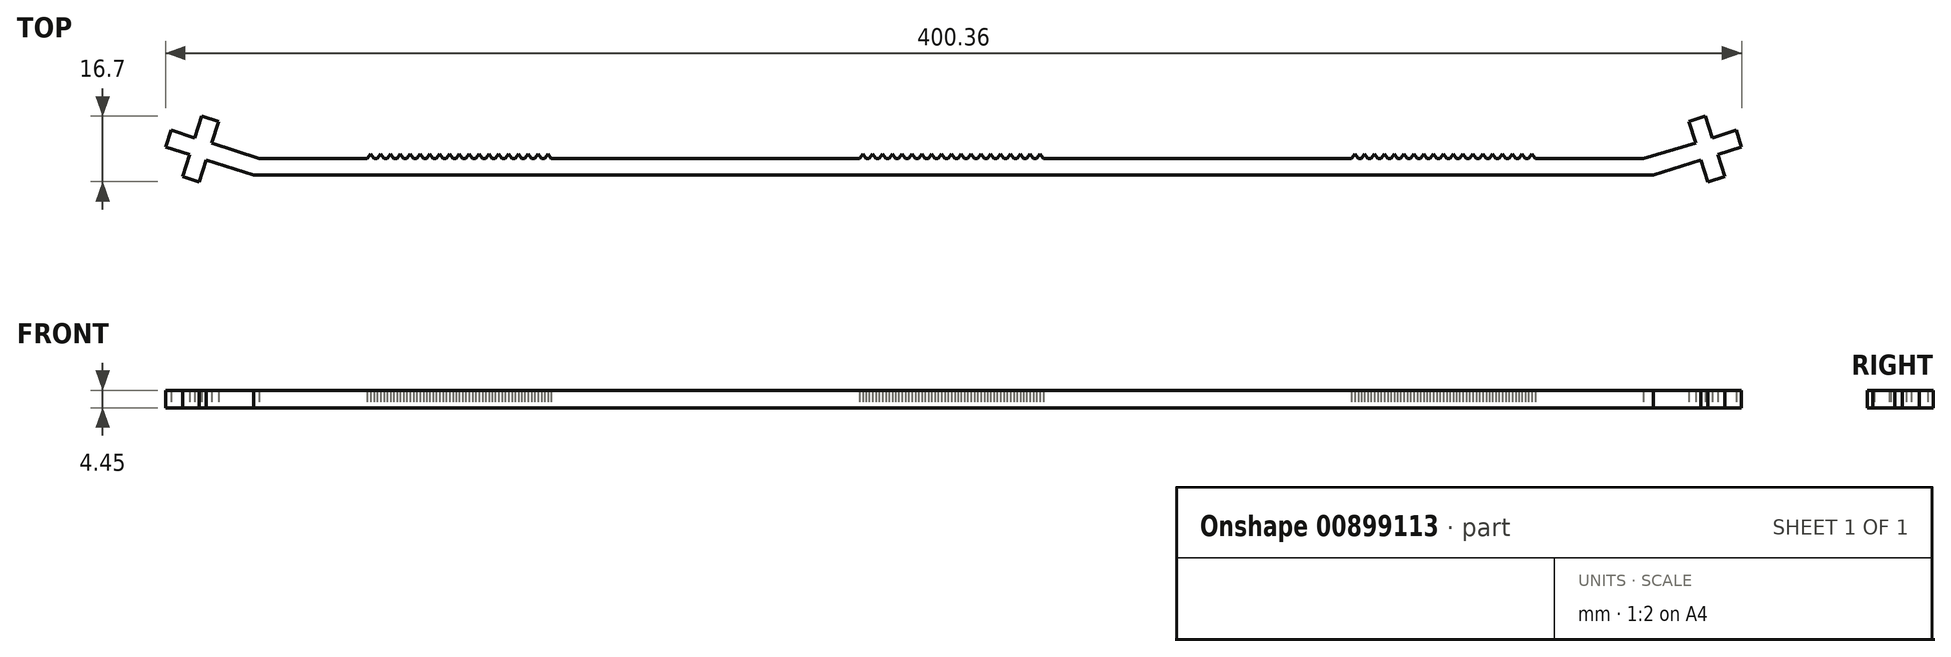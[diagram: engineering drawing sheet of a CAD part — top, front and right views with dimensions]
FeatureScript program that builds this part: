
annotation { "Feature Type Name" : "Feature", "Feature Type Description" : "" }
export const myFeature = defineFeature(function(context is Context, id is Id, definition is map)
    precondition{}
    {
        {
            var Q0;
            Q0=qCreatedBy(makeId("Top.planeOp"),FACE);
            var sketch = newSketch(context, id + "F0", { "sketchPlane" : qUnion([Q0])});
            skLineSegment(sketch, "E0", {"start": v(-319.35, 28.42) * mm, "end": v(36.25, 28.42) * mm});
            skLineSegment(sketch, "E1", {"start": v(-319.35, 28.42) * mm, "end": v(-331.45, 32.3) * mm});
            skLineSegment(sketch, "E2", {"start": v(-331.45, 32.3) * mm, "end": v(-333.23, 26.75) * mm});
            skLineSegment(sketch, "E3", {"start": v(-333.23, 26.75) * mm, "end": v(-337.46, 28.1) * mm});
            skLineSegment(sketch, "E4", {"start": v(-337.46, 28.1) * mm, "end": v(-335.68, 33.66) * mm});
            skLineSegment(sketch, "E5", {"start": v(-335.68, 33.66) * mm, "end": v(-341.73, 35.6) * mm});
            skLineSegment(sketch, "E6", {"start": v(-341.73, 35.6) * mm, "end": v(-340.37, 39.84) * mm});
            skLineSegment(sketch, "E7", {"start": v(-340.37, 39.84) * mm, "end": v(-334.32, 37.9) * mm});
            skLineSegment(sketch, "E8", {"start": v(-334.32, 37.9) * mm, "end": v(-332.54, 43.45) * mm});
            skLineSegment(sketch, "E9", {"start": v(-332.54, 43.45) * mm, "end": v(-328.3, 42.09) * mm});
            skLineSegment(sketch, "E10", {"start": v(-328.3, 42.09) * mm, "end": v(-330.09, 36.54) * mm});
            skLineSegment(sketch, "E11", {"start": v(-330.09, 36.54) * mm, "end": v(-318, 32.66) * mm});
            skLineSegment(sketch, "E12", {"start": v(-318, 32.66) * mm, "end": v(-290.5, 32.66) * mm});
            skLineSegment(sketch, "E13", {"start": v(-142.13, 33.8) * mm, "end": v(-141.27, 32.66) * mm});
            skLineSegment(sketch, "E14.MirrorCS", {"start": v(-142.13, 33.8) * mm, "end": v(-143, 32.66) * mm});
            skLineSegment(sketch, "E15.trimOffspring", {"start": v(-141.27, 32.66) * mm, "end": v(-140.5, 32.66) * mm});
            skPoint(sketch, "E16.start.orphan", {"position": v(-141.55, 28.42) * mm});
            skLineSegment(sketch, "E17.direction1", {"start": v(-141.27, 32.66) * mm, "end": v(-140.5, 32.66) * mm, "construction": true});
            skLineSegment(sketch, "E18.1.0.0", {"start": v(-139.63, 33.8) * mm, "end": v(-138.77, 32.66) * mm});
            skLineSegment(sketch, "E18.1.0.1", {"start": v(-139.63, 33.8) * mm, "end": v(-140.5, 32.66) * mm});
            skLineSegment(sketch, "E18.2.0.0", {"start": v(-137.13, 33.8) * mm, "end": v(-136.27, 32.66) * mm});
            skLineSegment(sketch, "E18.2.0.1", {"start": v(-137.13, 33.8) * mm, "end": v(-138, 32.66) * mm});
            skLineSegment(sketch, "E18.3.0.0", {"start": v(-134.63, 33.8) * mm, "end": v(-133.77, 32.66) * mm});
            skLineSegment(sketch, "E18.3.0.1", {"start": v(-134.63, 33.8) * mm, "end": v(-135.5, 32.66) * mm});
            skLineSegment(sketch, "E18.4.0.0", {"start": v(-132.13, 33.8) * mm, "end": v(-131.27, 32.66) * mm});
            skLineSegment(sketch, "E18.4.0.1", {"start": v(-132.13, 33.8) * mm, "end": v(-133, 32.66) * mm});
            skLineSegment(sketch, "E18.5.0.0", {"start": v(-129.63, 33.8) * mm, "end": v(-128.77, 32.66) * mm});
            skLineSegment(sketch, "E18.5.0.1", {"start": v(-129.63, 33.8) * mm, "end": v(-130.5, 32.66) * mm});
            skLineSegment(sketch, "E18.6.0.0", {"start": v(-127.13, 33.8) * mm, "end": v(-126.27, 32.66) * mm});
            skLineSegment(sketch, "E18.6.0.1", {"start": v(-127.13, 33.8) * mm, "end": v(-128, 32.66) * mm});
            skLineSegment(sketch, "E18.7.0.0", {"start": v(-124.63, 33.8) * mm, "end": v(-123.77, 32.66) * mm});
            skLineSegment(sketch, "E18.7.0.1", {"start": v(-124.63, 33.8) * mm, "end": v(-125.5, 32.66) * mm});
            skLineSegment(sketch, "E18.8.0.0", {"start": v(-122.13, 33.8) * mm, "end": v(-121.27, 32.66) * mm});
            skLineSegment(sketch, "E18.8.0.1", {"start": v(-122.13, 33.8) * mm, "end": v(-123, 32.66) * mm});
            skLineSegment(sketch, "E18.9.0.0", {"start": v(-119.63, 33.8) * mm, "end": v(-118.77, 32.66) * mm});
            skLineSegment(sketch, "E18.9.0.1", {"start": v(-119.63, 33.8) * mm, "end": v(-120.5, 32.66) * mm});
            skLineSegment(sketch, "E19.1.0.0", {"start": v(-144.63, 33.8) * mm, "end": v(-145.5, 32.66) * mm});
            skLineSegment(sketch, "E19.1.0.1", {"start": v(-144.63, 33.8) * mm, "end": v(-143.77, 32.66) * mm});
            skLineSegment(sketch, "E19.2.0.0", {"start": v(-147.13, 33.8) * mm, "end": v(-148, 32.66) * mm});
            skLineSegment(sketch, "E19.2.0.1", {"start": v(-147.13, 33.8) * mm, "end": v(-146.27, 32.66) * mm});
            skLineSegment(sketch, "E19.3.0.0", {"start": v(-149.63, 33.8) * mm, "end": v(-150.5, 32.66) * mm});
            skLineSegment(sketch, "E19.3.0.1", {"start": v(-149.63, 33.8) * mm, "end": v(-148.77, 32.66) * mm});
            skLineSegment(sketch, "E19.4.0.0", {"start": v(-152.13, 33.8) * mm, "end": v(-153, 32.66) * mm});
            skLineSegment(sketch, "E19.4.0.1", {"start": v(-152.13, 33.8) * mm, "end": v(-151.27, 32.66) * mm});
            skLineSegment(sketch, "E19.5.0.0", {"start": v(-154.63, 33.8) * mm, "end": v(-155.5, 32.66) * mm});
            skLineSegment(sketch, "E19.5.0.1", {"start": v(-154.63, 33.8) * mm, "end": v(-153.77, 32.66) * mm});
            skLineSegment(sketch, "E19.6.0.0", {"start": v(-157.13, 33.8) * mm, "end": v(-158, 32.66) * mm});
            skLineSegment(sketch, "E19.6.0.1", {"start": v(-157.13, 33.8) * mm, "end": v(-156.27, 32.66) * mm});
            skLineSegment(sketch, "E19.7.0.0", {"start": v(-159.63, 33.8) * mm, "end": v(-160.5, 32.66) * mm});
            skLineSegment(sketch, "E19.7.0.1", {"start": v(-159.63, 33.8) * mm, "end": v(-158.77, 32.66) * mm});
            skLineSegment(sketch, "E19.8.0.0", {"start": v(-162.13, 33.8) * mm, "end": v(-163, 32.66) * mm});
            skLineSegment(sketch, "E19.8.0.1", {"start": v(-162.13, 33.8) * mm, "end": v(-161.27, 32.66) * mm});
            skLineSegment(sketch, "E19.9.0.0", {"start": v(-164.63, 33.8) * mm, "end": v(-165.5, 32.66) * mm});
            skLineSegment(sketch, "E19.9.0.1", {"start": v(-164.63, 33.8) * mm, "end": v(-163.77, 32.66) * mm});
            skLineSegment(sketch, "E19.direction1", {"start": v(-143, 32.66) * mm, "end": v(-143.77, 32.66) * mm, "construction": true});
            skLineSegment(sketch, "E20.trimOffspring", {"start": v(-163.77, 32.66) * mm, "end": v(-163, 32.66) * mm});
            skLineSegment(sketch, "E21.trimOffspring", {"start": v(-161.27, 32.66) * mm, "end": v(-160.5, 32.66) * mm});
            skLineSegment(sketch, "E22.trimOffspring", {"start": v(-158.77, 32.66) * mm, "end": v(-158, 32.66) * mm});
            skLineSegment(sketch, "E23.trimOffspring", {"start": v(-153.77, 32.66) * mm, "end": v(-153, 32.66) * mm});
            skLineSegment(sketch, "E24.trimOffspring", {"start": v(-156.27, 32.66) * mm, "end": v(-155.5, 32.66) * mm});
            skLineSegment(sketch, "E25.trimOffspring", {"start": v(-151.27, 32.66) * mm, "end": v(-150.5, 32.66) * mm});
            skLineSegment(sketch, "E26.trimOffspring", {"start": v(-148.77, 32.66) * mm, "end": v(-148, 32.66) * mm});
            skLineSegment(sketch, "E27.trimOffspring", {"start": v(-146.27, 32.66) * mm, "end": v(-145.5, 32.66) * mm});
            skLineSegment(sketch, "E28.trimOffspring", {"start": v(-143.77, 32.66) * mm, "end": v(-143, 32.66) * mm});
            skLineSegment(sketch, "E29.trimOffspring", {"start": v(-138.77, 32.66) * mm, "end": v(-138, 32.66) * mm, "construction": true});
            skLineSegment(sketch, "E30.trimOffspring", {"start": v(-138.77, 32.66) * mm, "end": v(-138, 32.66) * mm});
            skLineSegment(sketch, "E31.trimOffspring", {"start": v(-136.27, 32.66) * mm, "end": v(-135.5, 32.66) * mm, "construction": true});
            skLineSegment(sketch, "E32.trimOffspring", {"start": v(-136.27, 32.66) * mm, "end": v(-135.5, 32.66) * mm});
            skLineSegment(sketch, "E33.trimOffspring", {"start": v(-133.77, 32.66) * mm, "end": v(-133, 32.66) * mm, "construction": true});
            skLineSegment(sketch, "E34.trimOffspring", {"start": v(-131.27, 32.66) * mm, "end": v(-130.5, 32.66) * mm, "construction": true});
            skLineSegment(sketch, "E35.trimOffspring", {"start": v(-131.27, 32.66) * mm, "end": v(-130.5, 32.66) * mm});
            skLineSegment(sketch, "E36", {"start": v(-133.77, 32.66) * mm, "end": v(-133, 32.66) * mm});
            skLineSegment(sketch, "E37.trimOffspring", {"start": v(-128.77, 32.66) * mm, "end": v(-128, 32.66) * mm, "construction": true});
            skLineSegment(sketch, "E38.trimOffspring", {"start": v(-128.77, 32.66) * mm, "end": v(-128, 32.66) * mm});
            skLineSegment(sketch, "E39.trimOffspring", {"start": v(-126.27, 32.66) * mm, "end": v(-125.5, 32.66) * mm, "construction": true});
            skLineSegment(sketch, "E40.trimOffspring", {"start": v(-126.27, 32.66) * mm, "end": v(-125.5, 32.66) * mm});
            skLineSegment(sketch, "E41.trimOffspring", {"start": v(-123.77, 32.66) * mm, "end": v(-123, 32.66) * mm, "construction": true});
            skLineSegment(sketch, "E42.trimOffspring", {"start": v(-123.77, 32.66) * mm, "end": v(-123, 32.66) * mm});
            skLineSegment(sketch, "E43.trimOffspring", {"start": v(-121.27, 32.66) * mm, "end": v(-120.5, 32.66) * mm, "construction": true});
            skLineSegment(sketch, "E44.trimOffspring", {"start": v(-121.27, 32.66) * mm, "end": v(-120.5, 32.66) * mm});
            skLineSegment(sketch, "E45.trimOffspring", {"start": v(-118.77, 32.66) * mm, "end": v(-116.27, 32.66) * mm, "construction": true});
            skLineSegment(sketch, "E46.trimOffspring", {"start": v(-118.77, 32.66) * mm, "end": v(-40.5, 32.66) * mm});
            skLineSegment(sketch, "E47.1.0.0", {"start": v(5.37, 33.8) * mm, "end": v(6.23, 32.66) * mm});
            skLineSegment(sketch, "E47.1.0.1", {"start": v(5.37, 33.8) * mm, "end": v(4.5, 32.66) * mm});
            skLineSegment(sketch, "E47.1.0.2", {"start": v(2.87, 33.8) * mm, "end": v(3.73, 32.66) * mm});
            skLineSegment(sketch, "E47.1.0.3", {"start": v(2.87, 33.8) * mm, "end": v(2, 32.66) * mm});
            skLineSegment(sketch, "E47.1.0.4", {"start": v(0.37, 33.8) * mm, "end": v(1.23, 32.66) * mm});
            skLineSegment(sketch, "E47.1.0.5", {"start": v(0.37, 33.8) * mm, "end": v(-0.5, 32.66) * mm});
            skLineSegment(sketch, "E47.1.0.6", {"start": v(-2.13, 33.8) * mm, "end": v(-1.27, 32.66) * mm});
            skLineSegment(sketch, "E47.1.0.7", {"start": v(-2.13, 33.8) * mm, "end": v(-3, 32.66) * mm});
            skLineSegment(sketch, "E47.1.0.8", {"start": v(-4.63, 33.8) * mm, "end": v(-3.77, 32.66) * mm});
            skLineSegment(sketch, "E47.1.0.9", {"start": v(-4.63, 33.8) * mm, "end": v(-5.5, 32.66) * mm});
            skLineSegment(sketch, "E47.1.0.10", {"start": v(-7.13, 33.8) * mm, "end": v(-6.27, 32.66) * mm});
            skLineSegment(sketch, "E47.1.0.11", {"start": v(-7.13, 33.8) * mm, "end": v(-8, 32.66) * mm});
            skLineSegment(sketch, "E47.1.0.12", {"start": v(-9.63, 33.8) * mm, "end": v(-8.77, 32.66) * mm});
            skLineSegment(sketch, "E47.1.0.13", {"start": v(-9.63, 33.8) * mm, "end": v(-10.5, 32.66) * mm});
            skLineSegment(sketch, "E47.1.0.14", {"start": v(-12.13, 33.8) * mm, "end": v(-11.27, 32.66) * mm});
            skLineSegment(sketch, "E47.1.0.15", {"start": v(-12.13, 33.8) * mm, "end": v(-13, 32.66) * mm});
            skLineSegment(sketch, "E47.1.0.16", {"start": v(-14.63, 33.8) * mm, "end": v(-13.77, 32.66) * mm});
            skLineSegment(sketch, "E47.1.0.17", {"start": v(-14.63, 33.8) * mm, "end": v(-15.5, 32.66) * mm});
            skLineSegment(sketch, "E47.1.0.18", {"start": v(-17.13, 33.8) * mm, "end": v(-16.27, 32.66) * mm});
            skLineSegment(sketch, "E47.1.0.19", {"start": v(-17.13, 33.8) * mm, "end": v(-18, 32.66) * mm});
            skLineSegment(sketch, "E47.1.0.20", {"start": v(-19.63, 33.8) * mm, "end": v(-18.77, 32.66) * mm});
            skLineSegment(sketch, "E47.1.0.21", {"start": v(-19.63, 33.8) * mm, "end": v(-20.5, 32.66) * mm});
            skLineSegment(sketch, "E47.1.0.22", {"start": v(-22.13, 33.8) * mm, "end": v(-21.27, 32.66) * mm});
            skLineSegment(sketch, "E47.1.0.23", {"start": v(-22.13, 33.8) * mm, "end": v(-23, 32.66) * mm});
            skLineSegment(sketch, "E47.1.0.24", {"start": v(-24.63, 33.8) * mm, "end": v(-23.77, 32.66) * mm});
            skLineSegment(sketch, "E47.1.0.25", {"start": v(-24.63, 33.8) * mm, "end": v(-25.5, 32.66) * mm});
            skLineSegment(sketch, "E47.1.0.26", {"start": v(-27.13, 33.8) * mm, "end": v(-26.27, 32.66) * mm});
            skLineSegment(sketch, "E47.1.0.27", {"start": v(-27.13, 33.8) * mm, "end": v(-28, 32.66) * mm});
            skLineSegment(sketch, "E47.1.0.28", {"start": v(-29.63, 33.8) * mm, "end": v(-28.77, 32.66) * mm});
            skLineSegment(sketch, "E47.1.0.29", {"start": v(-29.63, 33.8) * mm, "end": v(-30.5, 32.66) * mm});
            skLineSegment(sketch, "E47.1.0.30", {"start": v(-32.13, 33.8) * mm, "end": v(-31.27, 32.66) * mm});
            skLineSegment(sketch, "E47.1.0.31", {"start": v(-32.13, 33.8) * mm, "end": v(-33, 32.66) * mm});
            skLineSegment(sketch, "E47.1.0.32", {"start": v(-34.63, 33.8) * mm, "end": v(-33.77, 32.66) * mm});
            skLineSegment(sketch, "E47.1.0.33", {"start": v(-34.63, 33.8) * mm, "end": v(-35.5, 32.66) * mm});
            skLineSegment(sketch, "E47.1.0.34", {"start": v(-37.13, 33.8) * mm, "end": v(-36.27, 32.66) * mm});
            skLineSegment(sketch, "E47.1.0.35", {"start": v(-37.13, 33.8) * mm, "end": v(-38, 32.66) * mm});
            skLineSegment(sketch, "E47.1.0.36", {"start": v(-39.63, 33.8) * mm, "end": v(-38.77, 32.66) * mm});
            skLineSegment(sketch, "E47.1.0.37", {"start": v(-39.63, 33.8) * mm, "end": v(-40.5, 32.66) * mm});
            skLineSegment(sketch, "E48.1.0.0", {"start": v(-244.63, 33.8) * mm, "end": v(-243.77, 32.66) * mm});
            skLineSegment(sketch, "E48.1.0.1", {"start": v(-244.63, 33.8) * mm, "end": v(-245.5, 32.66) * mm});
            skLineSegment(sketch, "E48.1.0.2", {"start": v(-247.13, 33.8) * mm, "end": v(-246.27, 32.66) * mm});
            skLineSegment(sketch, "E48.1.0.3", {"start": v(-247.13, 33.8) * mm, "end": v(-248, 32.66) * mm});
            skLineSegment(sketch, "E48.1.0.4", {"start": v(-249.63, 33.8) * mm, "end": v(-248.77, 32.66) * mm});
            skLineSegment(sketch, "E48.1.0.5", {"start": v(-249.63, 33.8) * mm, "end": v(-250.5, 32.66) * mm});
            skLineSegment(sketch, "E48.1.0.6", {"start": v(-252.13, 33.8) * mm, "end": v(-251.27, 32.66) * mm});
            skLineSegment(sketch, "E48.1.0.7", {"start": v(-252.13, 33.8) * mm, "end": v(-253, 32.66) * mm});
            skLineSegment(sketch, "E48.1.0.8", {"start": v(-254.63, 33.8) * mm, "end": v(-253.77, 32.66) * mm});
            skLineSegment(sketch, "E48.1.0.9", {"start": v(-254.63, 33.8) * mm, "end": v(-255.5, 32.66) * mm});
            skLineSegment(sketch, "E48.1.0.10", {"start": v(-257.13, 33.8) * mm, "end": v(-256.27, 32.66) * mm});
            skLineSegment(sketch, "E48.1.0.11", {"start": v(-257.13, 33.8) * mm, "end": v(-258, 32.66) * mm});
            skLineSegment(sketch, "E48.1.0.12", {"start": v(-259.63, 33.8) * mm, "end": v(-258.77, 32.66) * mm});
            skLineSegment(sketch, "E48.1.0.13", {"start": v(-259.63, 33.8) * mm, "end": v(-260.5, 32.66) * mm});
            skLineSegment(sketch, "E48.1.0.14", {"start": v(-262.13, 33.8) * mm, "end": v(-261.27, 32.66) * mm});
            skLineSegment(sketch, "E48.1.0.15", {"start": v(-262.13, 33.8) * mm, "end": v(-263, 32.66) * mm});
            skLineSegment(sketch, "E48.1.0.16", {"start": v(-264.63, 33.8) * mm, "end": v(-263.77, 32.66) * mm});
            skLineSegment(sketch, "E48.1.0.17", {"start": v(-264.63, 33.8) * mm, "end": v(-265.5, 32.66) * mm});
            skLineSegment(sketch, "E48.1.0.18", {"start": v(-267.13, 33.8) * mm, "end": v(-266.27, 32.66) * mm});
            skLineSegment(sketch, "E48.1.0.19", {"start": v(-267.13, 33.8) * mm, "end": v(-268, 32.66) * mm});
            skLineSegment(sketch, "E48.1.0.20", {"start": v(-289.63, 33.8) * mm, "end": v(-290.5, 32.66) * mm});
            skLineSegment(sketch, "E48.1.0.21", {"start": v(-289.63, 33.8) * mm, "end": v(-288.77, 32.66) * mm});
            skLineSegment(sketch, "E48.1.0.22", {"start": v(-287.13, 33.8) * mm, "end": v(-288, 32.66) * mm});
            skLineSegment(sketch, "E48.1.0.23", {"start": v(-287.13, 33.8) * mm, "end": v(-286.27, 32.66) * mm});
            skLineSegment(sketch, "E48.1.0.24", {"start": v(-284.63, 33.8) * mm, "end": v(-285.5, 32.66) * mm});
            skLineSegment(sketch, "E48.1.0.25", {"start": v(-284.63, 33.8) * mm, "end": v(-283.77, 32.66) * mm});
            skLineSegment(sketch, "E48.1.0.26", {"start": v(-282.13, 33.8) * mm, "end": v(-283, 32.66) * mm});
            skLineSegment(sketch, "E48.1.0.27", {"start": v(-282.13, 33.8) * mm, "end": v(-281.27, 32.66) * mm});
            skLineSegment(sketch, "E48.1.0.28", {"start": v(-279.63, 33.8) * mm, "end": v(-280.5, 32.66) * mm});
            skLineSegment(sketch, "E48.1.0.29", {"start": v(-279.63, 33.8) * mm, "end": v(-278.77, 32.66) * mm});
            skLineSegment(sketch, "E48.1.0.30", {"start": v(-277.13, 33.8) * mm, "end": v(-278, 32.66) * mm});
            skLineSegment(sketch, "E48.1.0.31", {"start": v(-277.13, 33.8) * mm, "end": v(-276.27, 32.66) * mm});
            skLineSegment(sketch, "E48.1.0.32", {"start": v(-274.63, 33.8) * mm, "end": v(-275.5, 32.66) * mm});
            skLineSegment(sketch, "E48.1.0.33", {"start": v(-274.63, 33.8) * mm, "end": v(-273.77, 32.66) * mm});
            skLineSegment(sketch, "E48.1.0.34", {"start": v(-272.13, 33.8) * mm, "end": v(-273, 32.66) * mm});
            skLineSegment(sketch, "E48.1.0.35", {"start": v(-272.13, 33.8) * mm, "end": v(-271.27, 32.66) * mm});
            skLineSegment(sketch, "E48.1.0.36", {"start": v(-269.63, 33.8) * mm, "end": v(-270.5, 32.66) * mm});
            skLineSegment(sketch, "E48.1.0.37", {"start": v(-269.63, 33.8) * mm, "end": v(-268.77, 32.66) * mm});
            skLineSegment(sketch, "E48.direction1", {"start": v(-118.77, 32.66) * mm, "end": v(-243.77, 32.66) * mm, "construction": true});
            skLineSegment(sketch, "E49.trimOffspring", {"start": v(-288.77, 32.66) * mm, "end": v(-288, 32.66) * mm});
            skLineSegment(sketch, "E50.trimOffspring", {"start": v(-286.27, 32.66) * mm, "end": v(-285.5, 32.66) * mm});
            skLineSegment(sketch, "E51.trimOffspring", {"start": v(-283.77, 32.66) * mm, "end": v(-283, 32.66) * mm});
            skLineSegment(sketch, "E52.trimOffspring", {"start": v(-281.27, 32.66) * mm, "end": v(-280.5, 32.66) * mm});
            skLineSegment(sketch, "E53.trimOffspring", {"start": v(-278.77, 32.66) * mm, "end": v(-278, 32.66) * mm});
            skLineSegment(sketch, "E54.trimOffspring", {"start": v(-276.27, 32.66) * mm, "end": v(-275.5, 32.66) * mm});
            skLineSegment(sketch, "E55.trimOffspring", {"start": v(-273.77, 32.66) * mm, "end": v(-273, 32.66) * mm});
            skLineSegment(sketch, "E56.trimOffspring", {"start": v(-271.27, 32.66) * mm, "end": v(-270.5, 32.66) * mm});
            skLineSegment(sketch, "E57.trimOffspring", {"start": v(-268.77, 32.66) * mm, "end": v(-268, 32.66) * mm});
            skLineSegment(sketch, "E58.trimOffspring", {"start": v(-266.27, 32.66) * mm, "end": v(-265.5, 32.66) * mm});
            skLineSegment(sketch, "E59.trimOffspring", {"start": v(-263.77, 32.66) * mm, "end": v(-263, 32.66) * mm});
            skLineSegment(sketch, "E60.trimOffspring", {"start": v(-261.27, 32.66) * mm, "end": v(-260.5, 32.66) * mm});
            skLineSegment(sketch, "E61.trimOffspring", {"start": v(-258.77, 32.66) * mm, "end": v(-258, 32.66) * mm});
            skLineSegment(sketch, "E62.trimOffspring", {"start": v(-256.27, 32.66) * mm, "end": v(-255.5, 32.66) * mm});
            skLineSegment(sketch, "E63.trimOffspring", {"start": v(-253.77, 32.66) * mm, "end": v(-253, 32.66) * mm});
            skLineSegment(sketch, "E64.trimOffspring", {"start": v(-251.27, 32.66) * mm, "end": v(-250.5, 32.66) * mm});
            skLineSegment(sketch, "E65.trimOffspring", {"start": v(-248.77, 32.66) * mm, "end": v(-248, 32.66) * mm});
            skLineSegment(sketch, "E66.trimOffspring", {"start": v(-246.27, 32.66) * mm, "end": v(-245.5, 32.66) * mm});
            skLineSegment(sketch, "E67.trimOffspring", {"start": v(-243.77, 32.66) * mm, "end": v(-165.5, 32.66) * mm});
            skLineSegment(sketch, "E68.trimOffspring", {"start": v(6.23, 32.66) * mm, "end": v(33.73, 32.66) * mm});
            skLineSegment(sketch, "E69.trimOffspring", {"start": v(3.73, 32.66) * mm, "end": v(4.5, 32.66) * mm, "construction": true});
            skLineSegment(sketch, "E70.trimOffspring", {"start": v(3.73, 32.66) * mm, "end": v(4.5, 32.66) * mm});
            skLineSegment(sketch, "E71.trimOffspring", {"start": v(1.23, 32.66) * mm, "end": v(2, 32.66) * mm, "construction": true});
            skLineSegment(sketch, "E72.trimOffspring", {"start": v(1.23, 32.66) * mm, "end": v(2, 32.66) * mm});
            skLineSegment(sketch, "E73.trimOffspring", {"start": v(-1.27, 32.66) * mm, "end": v(-0.5, 32.66) * mm, "construction": true});
            skLineSegment(sketch, "E74.trimOffspring", {"start": v(-1.27, 32.66) * mm, "end": v(-0.5, 32.66) * mm});
            skLineSegment(sketch, "E75.trimOffspring", {"start": v(-3.77, 32.66) * mm, "end": v(-3, 32.66) * mm, "construction": true});
            skLineSegment(sketch, "E76.trimOffspring", {"start": v(-3.77, 32.66) * mm, "end": v(-3, 32.66) * mm});
            skLineSegment(sketch, "E77.trimOffspring", {"start": v(-6.27, 32.66) * mm, "end": v(-5.5, 32.66) * mm});
            skLineSegment(sketch, "E78.trimOffspring", {"start": v(-8.77, 32.66) * mm, "end": v(-8, 32.66) * mm});
            skLineSegment(sketch, "E79.trimOffspring", {"start": v(-11.27, 32.66) * mm, "end": v(-10.5, 32.66) * mm});
            skLineSegment(sketch, "E80.trimOffspring", {"start": v(-13.77, 32.66) * mm, "end": v(-13, 32.66) * mm});
            skLineSegment(sketch, "E81.trimOffspring", {"start": v(-16.27, 32.66) * mm, "end": v(-15.5, 32.66) * mm});
            skLineSegment(sketch, "E82.trimOffspring", {"start": v(-18.77, 32.66) * mm, "end": v(-18, 32.66) * mm});
            skLineSegment(sketch, "E83.trimOffspring", {"start": v(-21.27, 32.66) * mm, "end": v(-20.5, 32.66) * mm});
            skLineSegment(sketch, "E84.trimOffspring", {"start": v(-23.77, 32.66) * mm, "end": v(-23, 32.66) * mm});
            skLineSegment(sketch, "E85.trimOffspring", {"start": v(-38.77, 32.66) * mm, "end": v(-38, 32.66) * mm});
            skLineSegment(sketch, "E86.trimOffspring", {"start": v(-36.27, 32.66) * mm, "end": v(-35.5, 32.66) * mm});
            skLineSegment(sketch, "E87.trimOffspring", {"start": v(-33.77, 32.66) * mm, "end": v(-33, 32.66) * mm});
            skLineSegment(sketch, "E88.trimOffspring", {"start": v(-31.27, 32.66) * mm, "end": v(-30.5, 32.66) * mm});
            skLineSegment(sketch, "E89.trimOffspring", {"start": v(-28.77, 32.66) * mm, "end": v(-28, 32.66) * mm});
            skLineSegment(sketch, "E90.trimOffspring", {"start": v(-26.27, 32.66) * mm, "end": v(-25.5, 32.66) * mm});
            skLineSegment(sketch, "E91.MirrorCS", {"start": v(57.27, 39.84) * mm, "end": v(51.22, 37.9) * mm});
            skLineSegment(sketch, "E92.MirrorCS", {"start": v(45.2, 42.09) * mm, "end": v(46.98, 36.54) * mm});
            skLineSegment(sketch, "E93.MirrorCS", {"start": v(46.98, 36.54) * mm, "end": v(33.73, 32.66) * mm});
            skLineSegment(sketch, "E94.MirrorCS", {"start": v(54.36, 28.1) * mm, "end": v(52.58, 33.66) * mm});
            skLineSegment(sketch, "E95.MirrorCS", {"start": v(49.44, 43.45) * mm, "end": v(45.2, 42.09) * mm});
            skLineSegment(sketch, "E96.MirrorCS", {"start": v(58.63, 35.6) * mm, "end": v(57.27, 39.84) * mm});
            skLineSegment(sketch, "E97.MirrorCS", {"start": v(52.58, 33.66) * mm, "end": v(58.63, 35.6) * mm});
            skLineSegment(sketch, "E98.MirrorCS", {"start": v(36.25, 28.42) * mm, "end": v(48.34, 32.3) * mm});
            skLineSegment(sketch, "E99.MirrorCS", {"start": v(50.12, 26.75) * mm, "end": v(54.36, 28.1) * mm});
            skLineSegment(sketch, "E100.MirrorCS", {"start": v(48.34, 32.3) * mm, "end": v(50.12, 26.75) * mm});
            skLineSegment(sketch, "E101.MirrorCS", {"start": v(51.22, 37.9) * mm, "end": v(49.44, 43.45) * mm});
            skSolve(sketch);
        }
        {
            var Q0;
            Q0=makeQuery(id+"F0.imprint","IMPRINT",FACE,{"disambiguationData":[TD([[makeQuery(id+"F0.imprint","IMPRINT",EDGE,{"derivedFrom":sQuery(id+"F0.wireOp",EDGE,"E0")}),1.0]])]});
            extrude(context, id + "F1", {"entities" : qUnion([Q0]), "depth" : 4.45 * mm, "offsetDistance" : 25 * mm});
        }
    });
